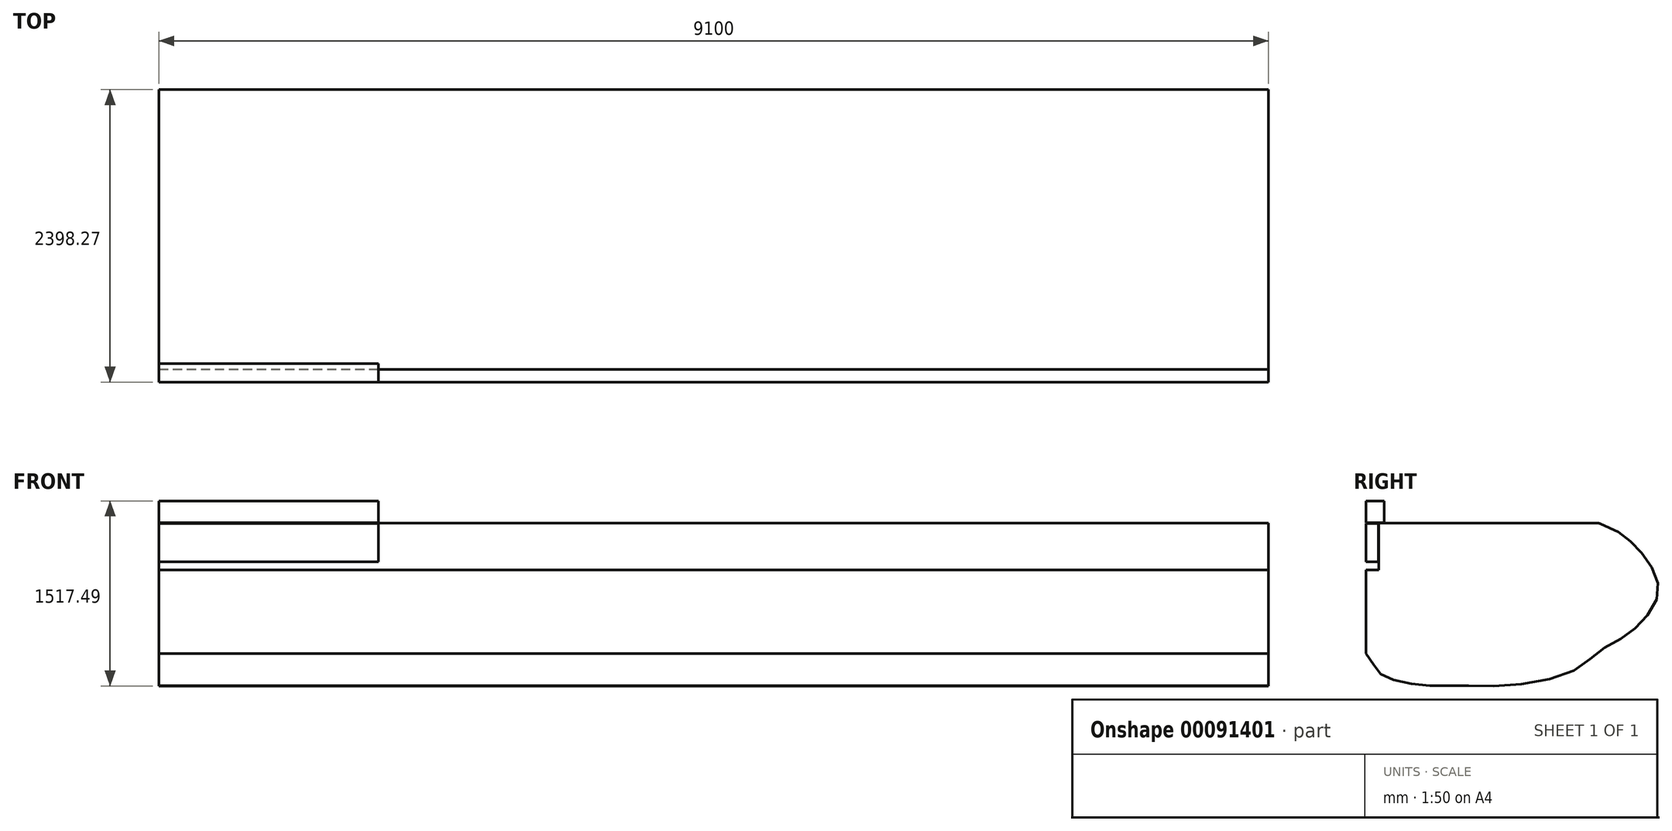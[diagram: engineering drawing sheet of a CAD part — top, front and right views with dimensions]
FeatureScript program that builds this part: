
annotation { "Feature Type Name" : "Feature", "Feature Type Description" : "" }
export const myFeature = defineFeature(function(context is Context, id is Id, definition is map)
    precondition{}
    {
        {
            var Q0;
            Q0=qCreatedBy(makeId("Right.planeOp"),FACE);
            var sketch = newSketch(context, id + "F0", { "sketchPlane" : qUnion([Q0])});
            skLineSegment(sketch, "E0.bottom", {"start": v(0, -289.12) * mm, "end": v(150, -289.12) * mm});
            skLineSegment(sketch, "E0.top", {"start": v(0, -469.12) * mm, "end": v(150, -469.12) * mm});
            skLineSegment(sketch, "E0.left", {"start": v(0, -289.12) * mm, "end": v(0, -469.12) * mm});
            skLineSegment(sketch, "E0.right", {"start": v(150, -289.12) * mm, "end": v(150, -469.12) * mm});
            skSolve(sketch);
        }
        {
            var Q0;
            Q0=qCreatedBy(makeId("Right.planeOp"),FACE);
            var sketch = newSketch(context, id + "F1", { "sketchPlane" : qUnion([Q0])});
            skLineSegment(sketch, "E1.top", {"start": v(0, -473.68) * mm, "end": v(101.53, -473.68) * mm});
            skLineSegment(sketch, "E1.left", {"start": v(0, -787.5) * mm, "end": v(0, -473.68) * mm});
            skLineSegment(sketch, "E1.right", {"start": v(101.53, -787.5) * mm, "end": v(101.53, -473.68) * mm});
            skLineSegment(sketch, "E2", {"start": v(0, -787.5) * mm, "end": v(101.53, -787.5) * mm});
            skSolve(sketch);
        }
        {
            var Q0;
            Q0 = qSketchRegion(id + "F0", true);
            extrude(context, id + "F2", {"entities" : qUnion([Q0]), "depth" : 1800 * mm});
        }
        {
            var Q0;
            Q0 = qSketchRegion(id + "F1", true);
            extrude(context, id + "F3", {"entities" : qUnion([Q0]), "depth" : 1800 * mm});
        }
        {
            var Q0;
            Q0=qCreatedBy(makeId("Right.planeOp"),FACE);
            var sketch = newSketch(context, id + "F4", { "sketchPlane" : qUnion([Q0])});
            skLineSegment(sketch, "E3.bottom", {"start": v(103.37, -470.76) * mm, "end": v(1892.88, -470.76) * mm});
            skLineSegment(sketch, "E3.left", {"start": v(103.37, -470.76) * mm, "end": v(103.37, -853.8) * mm});
            skLineSegment(sketch, "E4.left", {"start": v(0, -853.8) * mm, "end": v(0, -1540.58) * mm});
            skLineSegment(sketch, "E5", {"start": v(103.37, -853.8) * mm, "end": v(0, -853.8) * mm});
            skFitSpline(sketch, "E6", {"points": [v(1908.2, -470.76) * mm, v(2119.03, -580.72) * mm, v(2242.82, -693.9) * mm, v(2363.07, -874.27) * mm, v(2394.9, -1051.1) * mm, v(2288.8, -1252.7) * mm, v(2122.57, -1397.7) * mm, v(1920.98, -1517.94) * mm, v(1715.85, -1673.56) * mm, v(1221.99, -1797.79) * mm, v(775.49, -1804.08) * mm, v(527.09, -1804.08) * mm, v(284.97, -1772.63) * mm, v(130.9, -1716.03) * mm, v(71.16, -1646.86) * mm, v(0, -1540.58) * mm], "startDerivative": vector(4791.68, -1457.1) * mm, "endDerivative": vector(-1458.6, 2171.27) * mm});
            skArc(sketch, "E7.filletArc", {"start": v(1923.7, -475.63) * mm, "mid": v(1908.49, -471.98) * mm, "end": v(1892.88, -470.76) * mm});
            skSolve(sketch);
        }
        {
            var Q0;
            Q0 = qSketchRegion(id + "F4", true);
            extrude(context, id + "F5", {"entities" : qUnion([Q0]), "depth" : 9100 * mm});
        }
    });
